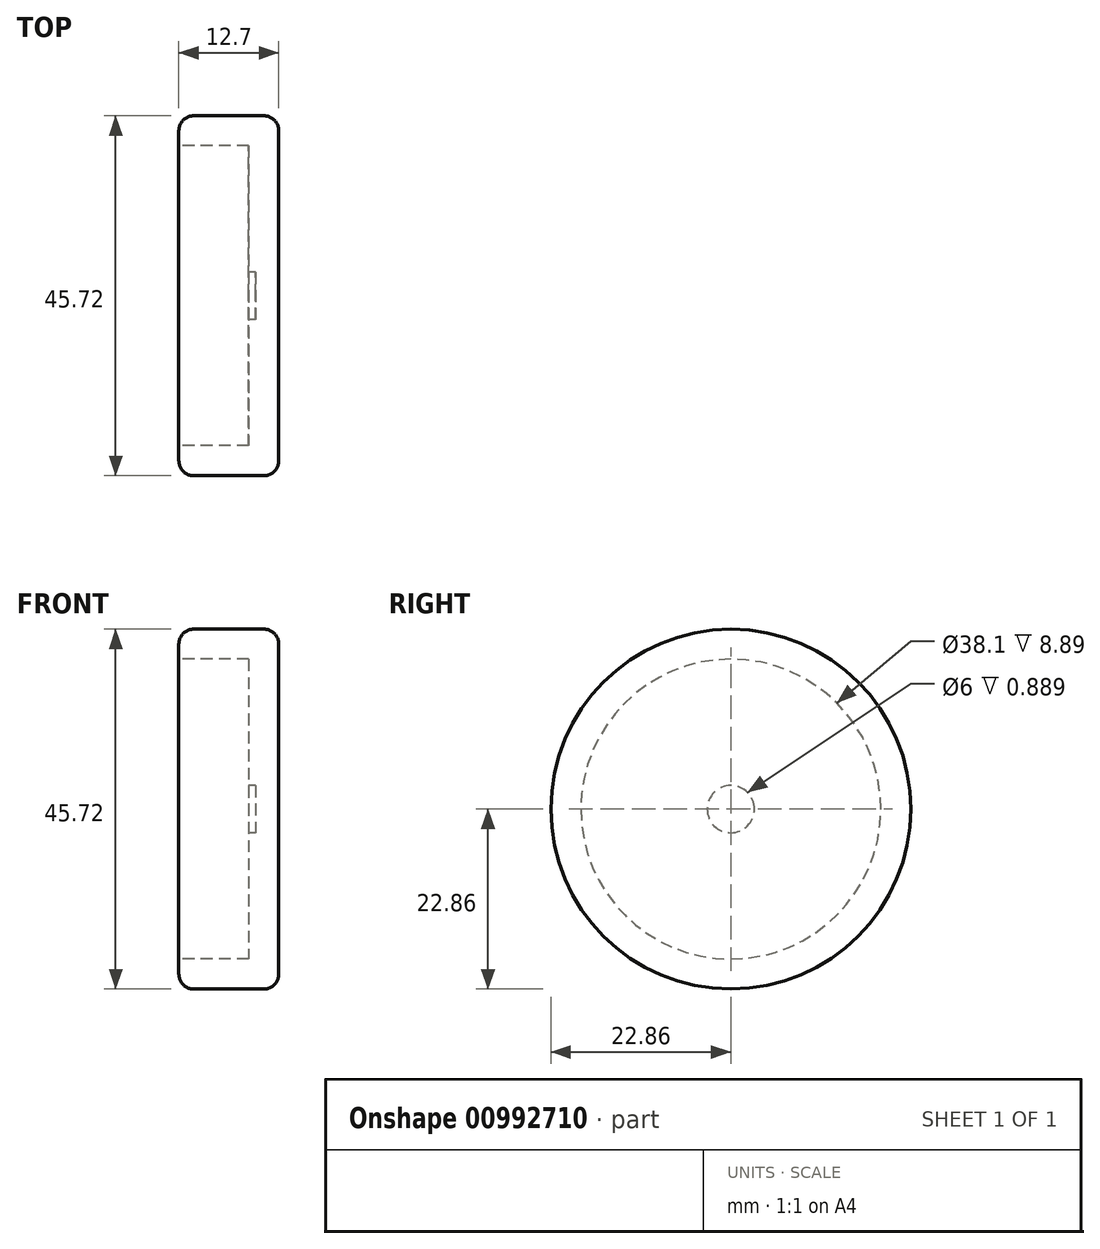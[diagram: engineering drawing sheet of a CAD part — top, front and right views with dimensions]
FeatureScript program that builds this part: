
annotation { "Feature Type Name" : "Feature", "Feature Type Description" : "" }
export const myFeature = defineFeature(function(context is Context, id is Id, definition is map)
    precondition{}
    {
        {
            var Q0;
            Q0=qCreatedBy(makeId("Front.planeOp"),FACE);
            var sketch = newSketch(context, id + "F0", { "sketchPlane" : qUnion([Q0])});
            skLineSegment(sketch, "E0", {"start": v(0, 19.05) * mm, "end": v(8.89, 19.05) * mm});
            skLineSegment(sketch, "E1", {"start": v(8.9, 19.05) * mm, "end": v(8.9, 0) * mm});
            skLineSegment(sketch, "E2", {"start": v(8.9, 0) * mm, "end": v(12.7, 0) * mm});
            skLineSegment(sketch, "E3", {"start": v(12.7, 0) * mm, "end": v(12.7, 20.96) * mm});
            skLineSegment(sketch, "E4", {"start": v(10.8, 22.86) * mm, "end": v(1.9, 22.86) * mm});
            skLineSegment(sketch, "E5", {"start": v(0, 20.96) * mm, "end": v(0, 19.05) * mm});
            skPoint(sketch, "E6.visualSharp", {"position": v(12.7, 22.86) * mm});
            skArc(sketch, "E6.filletArc", {"start": v(12.7, 20.96) * mm, "mid": v(12.14, 22.3) * mm, "end": v(10.8, 22.86) * mm});
            skPoint(sketch, "E7.visualSharp", {"position": v(0, 22.86) * mm});
            skArc(sketch, "E7.filletArc", {"start": v(1.9, 22.86) * mm, "mid": v(0.56, 22.3) * mm, "end": v(0, 20.96) * mm});
            skLineSegment(sketch, "E8", {"start": v(-7.84, 0) * mm, "end": v(12.7, 0) * mm, "construction": true});
            skSolve(sketch);
        }
        {
            var Q0;
            Q0=qSketchRegion(id+"F0",true);
            var Q1;
            Q1=sQuery(id+"F0.wireOp",EDGE,"E8");
            revolve(context, id + "F1", {"surfaceOperationType" : NewSurfaceOperationType.NEW, "entities" : qUnion([Q0]), "axis" : qUnion([Q1]), "revolveType" : RevolveType.FULL});
        }
        {
            var Q0;
            Q0=makeQuery(id+"F1.opRevolve","SWEPT_FACE",FACE,{"disambiguationData":[OSD([sQuery(id+"F0.wireOp",EDGE,"E1")])]});
            var sketch = newSketch(context, id + "F2", { "sketchPlane" : qUnion([Q0])});
            skCircle(sketch, "E9", {"center": v(0, 0) * mm, "radius": 3 * mm});
            skSolve(sketch);
        }
        {
            var Q0;
            Q0=qSketchRegion(id+"F2",true);
            extrude(context, id + "F3", {"entities" : qUnion([Q0]), "operationType" : NewBodyOperationType.REMOVE, "oppositeDirection" : true, "depth" : 0.89 * mm, "offsetDistance" : 25.4 * mm});
        }
    });
